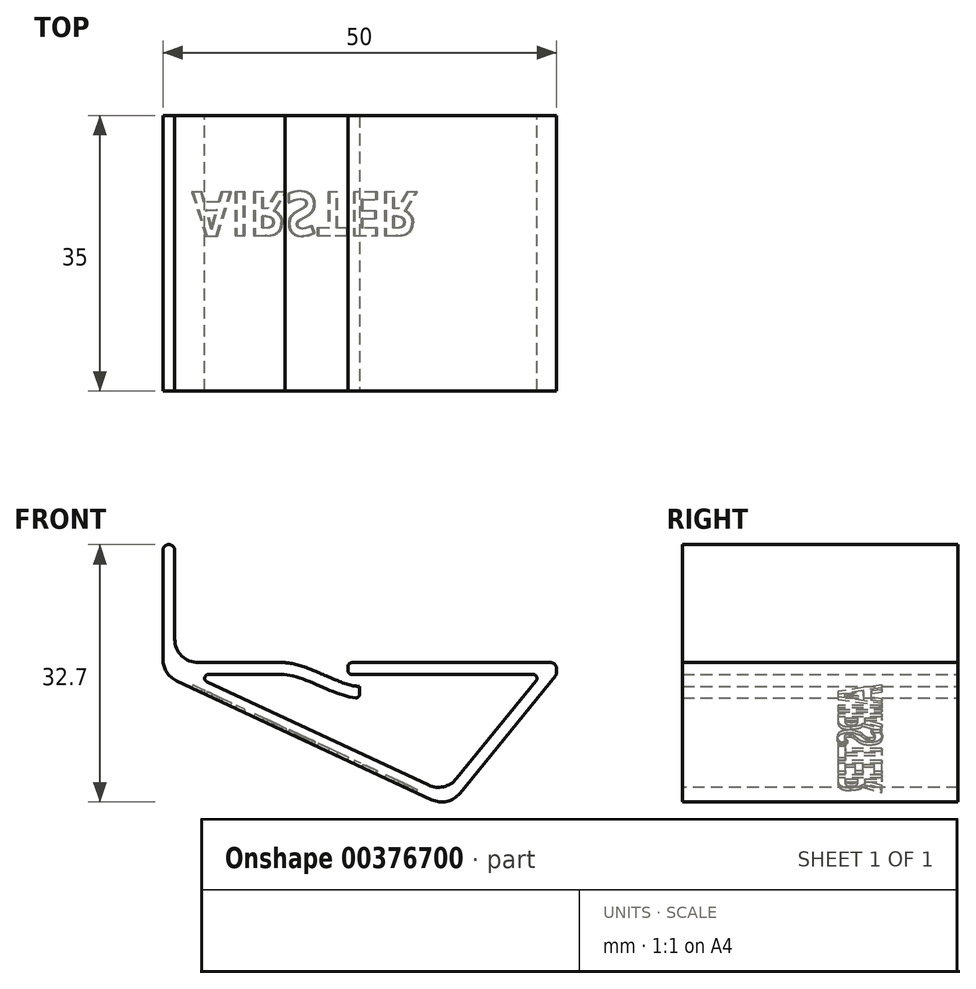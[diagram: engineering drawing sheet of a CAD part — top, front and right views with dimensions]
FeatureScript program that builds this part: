
annotation { "Feature Type Name" : "Feature", "Feature Type Description" : "" }
export const myFeature = defineFeature(function(context is Context, id is Id, definition is map)
    precondition{}
    {
        {
            var Q0;
            Q0=qCreatedBy(makeId("Front.planeOp"),FACE);
            var sketch = newSketch(context, id + "F0", { "sketchPlane" : qUnion([Q0])});
            skLineSegment(sketch, "E0.bottom", {"start": v(0, 1.5) * mm, "end": v(50, 1.5) * mm});
            skLineSegment(sketch, "E0.top", {"start": v(0, 0) * mm, "end": v(50, 0) * mm});
            skLineSegment(sketch, "E0.left", {"start": v(0, 1.5) * mm, "end": v(0, 0) * mm});
            skLineSegment(sketch, "E0.right", {"start": v(50, 1.5) * mm, "end": v(50, 0) * mm});
            skLineSegment(sketch, "E1.bottom", {"start": v(0, 16.5) * mm, "end": v(1.5, 16.5) * mm});
            skLineSegment(sketch, "E1.top", {"start": v(0, 1.5) * mm, "end": v(1.5, 1.5) * mm});
            skLineSegment(sketch, "E1.left", {"start": v(0, 16.5) * mm, "end": v(0, 1.5) * mm});
            skLineSegment(sketch, "E1.right", {"start": v(1.5, 16.5) * mm, "end": v(1.5, 1.5) * mm});
            skFitSpline(sketch, "E2", {"points": [v(25, -3) * mm, v(15, 0) * mm], "startDerivative": vector(-9, 0) * mm, "endDerivative": vector(-9, 0) * mm});
            skLineSegment(sketch, "E3", {"start": v(0, 0) * mm, "end": v(36.25, -16.9) * mm});
            skLineSegment(sketch, "E4", {"start": v(3.55, 0) * mm, "end": v(36.89, -15.55) * mm});
            skLineSegment(sketch, "E5", {"start": v(36.25, -16.9) * mm, "end": v(36.89, -15.55) * mm});
            skLineSegment(sketch, "E6", {"start": v(36.25, -16.9) * mm, "end": v(50, 0) * mm});
            skLineSegment(sketch, "E7", {"start": v(35.83, -15.05) * mm, "end": v(48.07, 0) * mm});
            skLineSegment(sketch, "E8", {"start": v(25, -3) * mm, "end": v(25, 1.5) * mm});
            skLineSegment(sketch, "E9.0", {"start": v(23.5, -1.24) * mm, "end": v(23.5, 1.5) * mm});
            skFitSpline(sketch, "E9.1", {"points": [v(25, -1.5) * mm, v(24.75, -1.5) * mm, v(24.16, -1.44) * mm, v(23.09, -1.13) * mm, v(21.89, -0.68) * mm, v(20.6, -0.13) * mm, v(19.26, 0.45) * mm, v(17.89, 0.97) * mm, v(16.48, 1.38) * mm, v(15.5, 1.5) * mm, v(15, 1.5) * mm]});
            skSolve(sketch);
        }
        {
            var Q0;
            Q0=makeQuery(id+"F0.imprint","IMPRINT",FACE,{"disambiguationData":[TD([[makeQuery(id+"F0.imprint","IMPRINT",EDGE,{"derivedFrom":sQuery(id+"F0.wireOp",EDGE,"E1.bottom")}),-1.0]])]});
            var Q1;
            {var subQ4=sQuery(id+"F0.wireOp",EDGE,"E0.left");Q1=makeQuery(id+"F0.imprint","IMPRINT",FACE,{"disambiguationData":[TD([[makeQuery(id+"F0.imprint","IMPRINT",EDGE,{"derivedFrom":subQ4}),1.0]])]});}
            var Q2;
            {var subQ1=sQuery(id+"F0.wireOp",EDGE,"E2");Q2=makeQuery(id+"F0.imprint","IMPRINT",FACE,{"disambiguationData":[TD([[makeQuery(id+"F0.imprint","IMPRINT",EDGE,{"derivedFrom":subQ1}),-1.0]])]});}
            var Q3;
            {var subQ0=sQuery(id+"F0.wireOp",EDGE,"E8");var subQ1=sQuery(id+"F0.wireOp",EDGE,"E0.bottom");var subQ2=makeQuery(id+"F0.imprint","INTERSECT",VERTEX,{"derivedFrom":[subQ1,subQ0]});Q3=makeQuery(id+"F0.imprint","IMPRINT",FACE,{"disambiguationData":[TD([[makeQuery(id+"F0.imprint","IMPRINT",EDGE,{"disambiguationData":[TD([[subQ2,1.0]])],"derivedFrom":subQ1}),-1.0]])]});}
            var Q4;
            {var subQ0=sQuery(id+"F0.wireOp",EDGE,"E0.right");Q4=makeQuery(id+"F0.imprint","IMPRINT",FACE,{"disambiguationData":[TD([[makeQuery(id+"F0.imprint","IMPRINT",EDGE,{"derivedFrom":subQ0}),-1.0]])]});}
            var Q5;
            {var subQ1=sQuery(id+"F0.wireOp",EDGE,"E5");Q5=makeQuery(id+"F0.imprint","IMPRINT",FACE,{"disambiguationData":[TD([[makeQuery(id+"F0.imprint","IMPRINT",EDGE,{"derivedFrom":subQ1}),-1.0]])]});}
            var Q6;
            {var subQ3=sQuery(id+"F0.wireOp",EDGE,"E3");Q6=makeQuery(id+"F0.imprint","IMPRINT",FACE,{"disambiguationData":[TD([[makeQuery(id+"F0.imprint","IMPRINT",EDGE,{"derivedFrom":subQ3}),1.0]])]});}
            extrude(context, id + "F1", {"entities" : qUnion([Q0, Q1, Q2, Q3, Q4, Q5, Q6]), "depth" : 35 * mm});
        }
        {
            var Q0;
            Q0=makeQuery(id+"F1.opExtrude","SWEPT_EDGE",EDGE,{"disambiguationData":[OSD([sQuery(id+"F0.wireOp",EDGE,"E0.bottom"),sQuery(id+"F0.wireOp",EDGE,"E1.top"),sQuery(id+"F0.wireOp",EDGE,"E1.right")])]});
            var Q1;
            Q1=makeQuery(id+"F1.opExtrude","SWEPT_EDGE",EDGE,{"disambiguationData":[OSD([sQuery(id+"F0.wireOp",EDGE,"E0.top"),sQuery(id+"F0.wireOp",EDGE,"E0.left"),sQuery(id+"F0.wireOp",EDGE,"E3")])]});
            var Q2;
            Q2=makeQuery(id+"F1.opExtrude","SWEPT_EDGE",EDGE,{"disambiguationData":[OSD([sQuery(id+"F0.wireOp",EDGE,"E3"),sQuery(id+"F0.wireOp",EDGE,"E5"),sQuery(id+"F0.wireOp",EDGE,"E6")])]});
            var Q3;
            Q3=makeQuery(id+"F1.opExtrude","SWEPT_EDGE",EDGE,{"disambiguationData":[OSD([sQuery(id+"F0.wireOp",EDGE,"E4"),sQuery(id+"F0.wireOp",EDGE,"E7")])]});
            fillet(context, id + "F2", {"entities" : qUnion([Q0, Q1, Q2, Q3]), "radius" : 3 * mm, "tangentPropagation" : true, "allowEdgeOverflow" : false});
        }
        {
            var Q0;
            Q0=makeQuery(id+"F1.opExtrude","SWEPT_EDGE",EDGE,{"disambiguationData":[OSD([sQuery(id+"F0.wireOp",EDGE,"E0.top"),sQuery(id+"F0.wireOp",EDGE,"E7")])]});
            var Q1;
            Q1=makeQuery(id+"F1.opExtrude","SWEPT_EDGE",EDGE,{"disambiguationData":[OSD([sQuery(id+"F0.wireOp",EDGE,"E0.top"),sQuery(id+"F0.wireOp",EDGE,"E4")])]});
            var Q2;
            Q2=makeQuery(id+"F1.opExtrude","SWEPT_EDGE",EDGE,{"disambiguationData":[OSD([sQuery(id+"F0.wireOp",EDGE,"E0.top"),sQuery(id+"F0.wireOp",EDGE,"aB5ngfBG-Lgge-cUuf-RRZt-Tg2LnY0Fz7UZ")])]});
            var Q3;
            Q3=makeQuery(id+"F1.opExtrude","SWEPT_EDGE",EDGE,{"disambiguationData":[OSD([sQuery(id+"F0.wireOp",EDGE,"aB5ngfBG-Lgge-cUuf-RRZt-Tg2LnY0Fz7UZ"),sQuery(id+"F0.wireOp",EDGE,"E2")])]});
            var Q4;
            Q4=makeQuery(id+"F1.opExtrude","SWEPT_EDGE",EDGE,{"disambiguationData":[OSD([sQuery(id+"F0.wireOp",EDGE,"E0.bottom"),sQuery(id+"F0.wireOp",EDGE,"E9.0")])]});
            fillet(context, id + "F3", {"entities" : qUnion([Q0, Q1, Q2, Q3, Q4]), "radius" : 0.5 * mm, "tangentPropagation" : true, "allowEdgeOverflow" : false});
        }
        {
            var Q0;
            Q0=makeQuery(id+"F1.opExtrude","SWEPT_EDGE",EDGE,{"disambiguationData":[OSD([sQuery(id+"F0.wireOp",EDGE,"E0.top"),sQuery(id+"F0.wireOp",EDGE,"E0.right"),sQuery(id+"F0.wireOp",EDGE,"E6")])]});
            var Q1;
            Q1=makeQuery(id+"F1.opExtrude","SWEPT_EDGE",EDGE,{"disambiguationData":[OSD([sQuery(id+"F0.wireOp",EDGE,"E0.bottom"),sQuery(id+"F0.wireOp",EDGE,"E0.right")])]});
            var Q2;
            Q2=makeQuery(id+"F1.opExtrude","SWEPT_EDGE",EDGE,{"disambiguationData":[OSD([sQuery(id+"F0.wireOp",EDGE,"E1.bottom"),sQuery(id+"F0.wireOp",EDGE,"E1.right")])]});
            var Q3;
            Q3=makeQuery(id+"F1.opExtrude","SWEPT_EDGE",EDGE,{"disambiguationData":[OSD([sQuery(id+"F0.wireOp",EDGE,"E1.bottom"),sQuery(id+"F0.wireOp",EDGE,"E1.left")])]});
            fillet(context, id + "F4", {"entities" : qUnion([Q0, Q1, Q2, Q3]), "radius" : 0.75 * mm, "tangentPropagation" : true, "allowEdgeOverflow" : false});
        }
        {
            var Q0;
            Q0=makeQuery(id+"F1.opExtrude","SWEPT_FACE",FACE,{"disambiguationData":[OSD([sQuery(id+"F0.wireOp",EDGE,"E3")])]});
            var sketch = newSketch(context, id + "F5", { "sketchPlane" : qUnion([Q0])});
            skText(sketch, "E10", { "text": "AIRSTER", "fontName": "OpenSans-Bold.ttf"});
            skPoint(sketch, "E11", {"position": v(35.79, 17.5) * mm});
            const initialGuessF5  = {"E10": [0.00404, 0.00969, 1, 0, 0.00562]};
            skSetInitialGuess(sketch, initialGuessF5);
            skSolve(sketch);
        }
        {
            var Q0;
            Q0=qSketchRegion(id+"F5",true);
            extrude(context, id + "F6", {"entities" : qUnion([Q0]), "operationType" : NewBodyOperationType.REMOVE, "oppositeDirection" : true, "depth" : 0.4 * mm});
        }
    });
